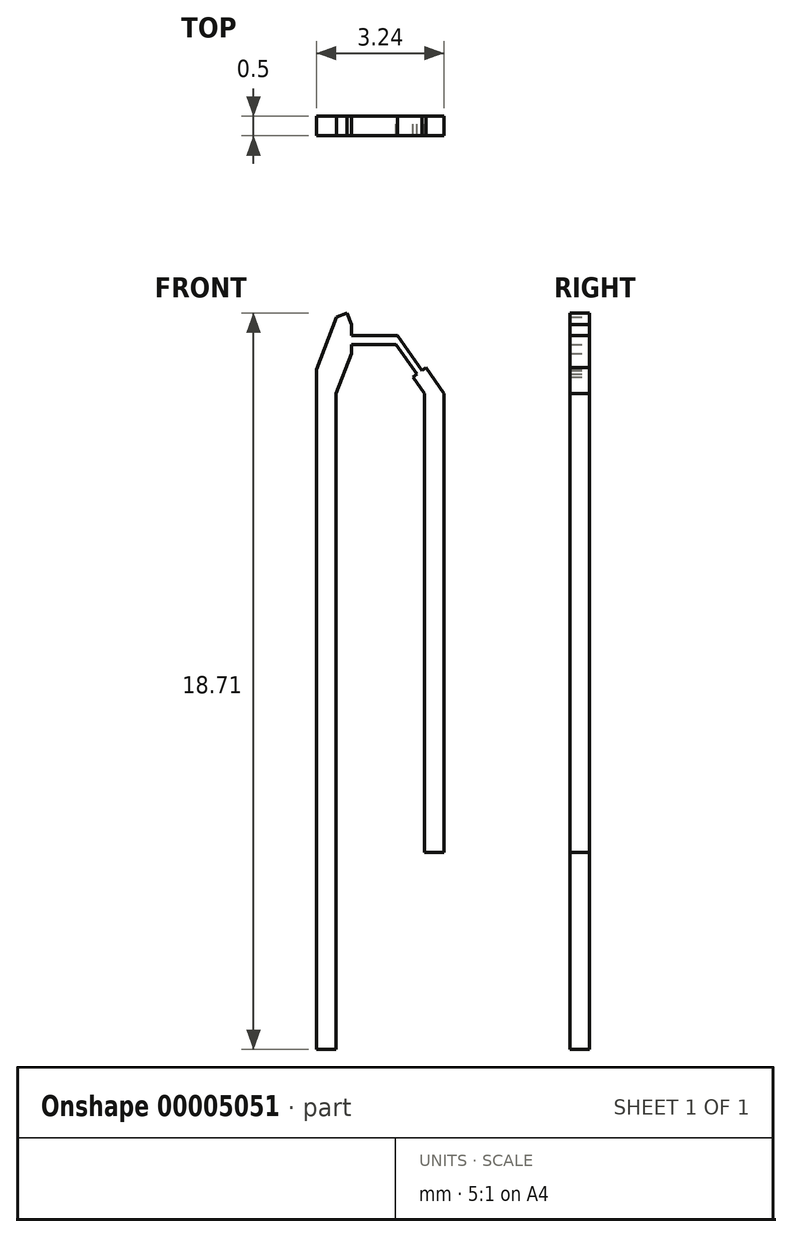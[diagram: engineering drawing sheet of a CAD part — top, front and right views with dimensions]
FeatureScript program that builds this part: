
annotation { "Feature Type Name" : "Feature", "Feature Type Description" : "" }
export const myFeature = defineFeature(function(context is Context, id is Id, definition is map)
    precondition{}
    {
        {
            var Q0;
            Q0=qCreatedBy(makeId("Front.planeOp"),FACE);
            var sketch = newSketch(context, id + "F0", { "sketchPlane" : qUnion([Q0])});
            skLineSegment(sketch, "E0", {"start": v(-3, 0) * mm, "end": v(3, 0) * mm, "construction": true});
            skLineSegment(sketch, "E1", {"start": v(-1.53, -15) * mm, "end": v(-1.53, 2.28) * mm});
            skLineSegment(sketch, "E2", {"start": v(-1.53, 2.28) * mm, "end": v(-1.02, 3.61) * mm});
            skLineSegment(sketch, "E3", {"start": v(-1.02, 3.61) * mm, "end": v(-0.75, 3.7) * mm});
            skLineSegment(sketch, "E4", {"start": v(-0.75, 3.7) * mm, "end": v(-0.65, 3.4) * mm});
            skLineSegment(sketch, "E5", {"start": v(-0.65, 3.4) * mm, "end": v(-0.65, 3.14) * mm});
            skLineSegment(sketch, "E6", {"start": v(-0.65, 2.68) * mm, "end": v(-1.03, 1.67) * mm});
            skLineSegment(sketch, "E7", {"start": v(-1.03, 1.67) * mm, "end": v(-1.03, -15) * mm});
            skLineSegment(sketch, "E8", {"start": v(-1.03, -15) * mm, "end": v(-1.53, -15) * mm});
            skLineSegment(sketch, "E9", {"start": v(1.2, -10) * mm, "end": v(1.2, 1.67) * mm});
            skPoint(sketch, "E9.startSnap0", {"position": v(-1.28, -15) * mm});
            skLineSegment(sketch, "E10", {"start": v(1.2, 1.67) * mm, "end": v(0.92, 2.08) * mm});
            skLineSegment(sketch, "E11", {"start": v(0.92, 2.08) * mm, "end": v(1.02, 2.15) * mm});
            skLineSegment(sketch, "E12", {"start": v(1.25, 2.32) * mm, "end": v(1.7, 1.67) * mm});
            skLineSegment(sketch, "E13", {"start": v(1.7, 1.67) * mm, "end": v(1.7, -10) * mm});
            skLineSegment(sketch, "E14", {"start": v(1.7, -10) * mm, "end": v(1.2, -10) * mm});
            skLineSegment(sketch, "E15", {"start": v(-0.65, 2.91) * mm, "end": v(0.49, 2.91) * mm});
            skLineSegment(sketch, "E16", {"start": v(0.49, 2.91) * mm, "end": v(1.02, 2.15) * mm});
            skLineSegment(sketch, "E17", {"start": v(-0.65, 3.14) * mm, "end": v(0.52, 3.14) * mm});
            skLineSegment(sketch, "E18", {"start": v(0.52, 3.14) * mm, "end": v(1.15, 2.24) * mm});
            skLineSegment(sketch, "E19.trimOffspring", {"start": v(-0.65, 2.91) * mm, "end": v(-0.65, 2.68) * mm});
            skLineSegment(sketch, "E20.trimOffspring", {"start": v(1.15, 2.24) * mm, "end": v(1.25, 2.32) * mm});
            skSolve(sketch);
        }
        {
            var Q0;
            Q0 = qSketchRegion(id + "F0", true);
            extrude(context, id + "F1", {"entities" : qUnion([Q0]), "depth" : 0.5 * mm, "symmetric" : true});
        }
    });
